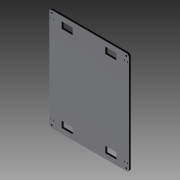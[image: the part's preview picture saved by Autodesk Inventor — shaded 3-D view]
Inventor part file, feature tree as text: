
AUTODESK INVENTOR PART (.ipt)
format: ipt  version: 2013 (Build 170138000, 138)  size: 199,168 bytes
history: native  units: in
note: dims shown in document units (in); Inventor stores cm internally (conversion verified against a paired STEP export)
features: extrude x3, sketch x3, fillet x1, reference x1
ambient origin geometry x8: Origin, YZ Plane, XZ Plane, XY Plane, X Axis, Y Axis, Z Axis, Center Point
feature tree (8):
  extrude  "Extrusion3"  Depth=8.8976in
  extrude  "Extrusion4"  Depth=0.3937in
  extrude  "Extrusion5"  Depth=0.225in TaperAngle=0.0deg
  fillet  "Fillet1"  Radius=0.1969in
  sketch  "Sketch3"  dims[d6=0.225in d7=0.0in d8=8.8976in]
  reference  "Reference2"
  sketch  "Sketch4"  dims[d10=0.225in d11=0.0in d12=0.3937in]
  sketch  "Sketch5"  dims[d15=0.7874in d16=0.225in d17=0.0in d18=0.1969in]
